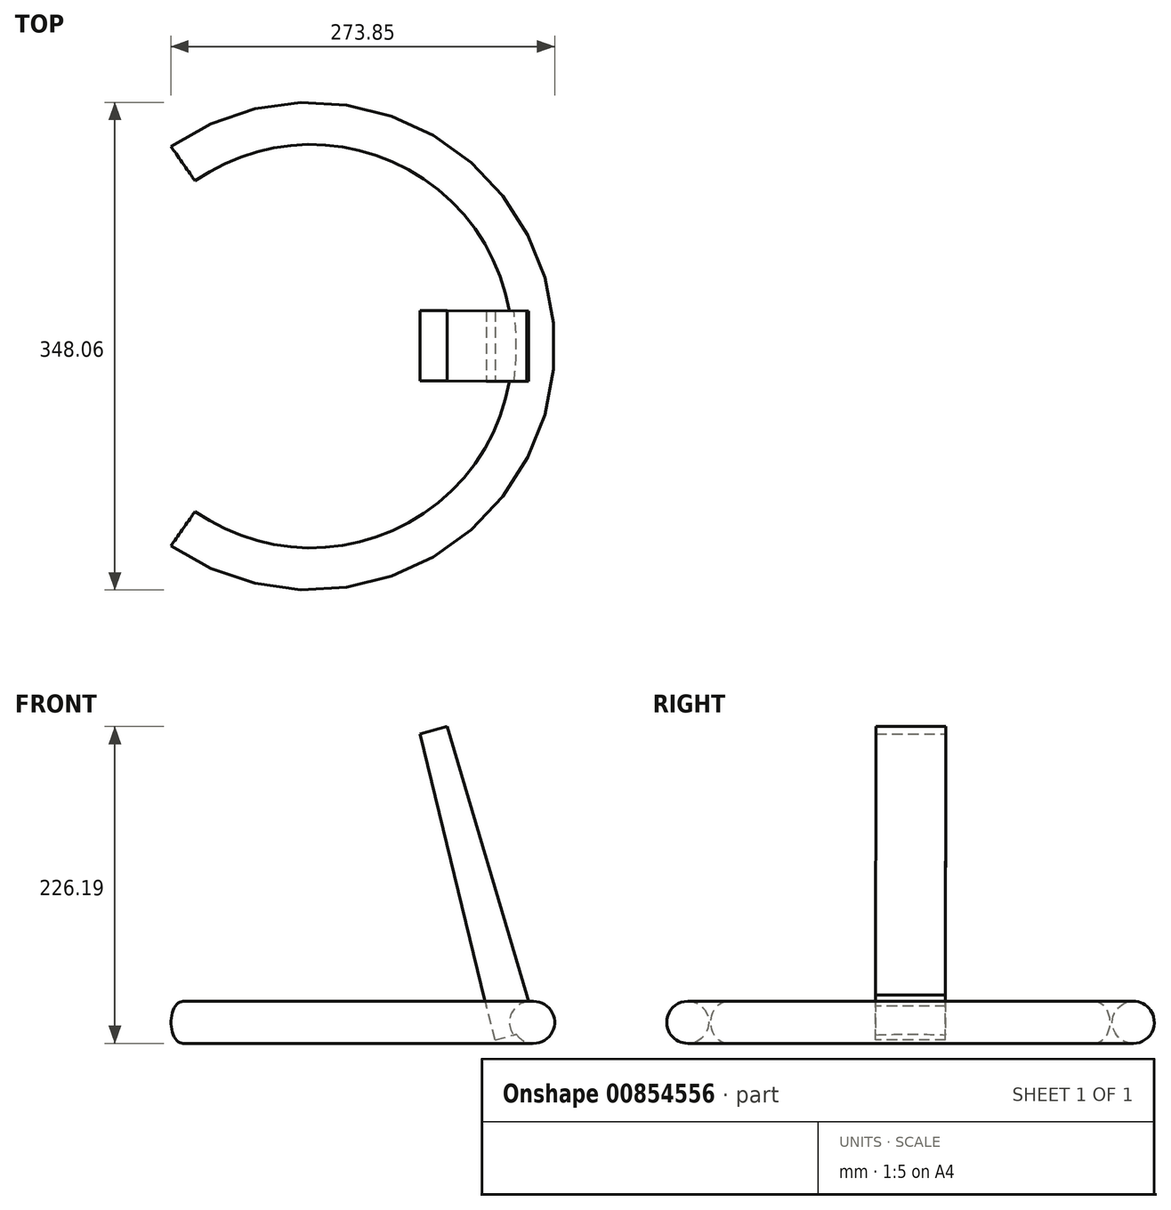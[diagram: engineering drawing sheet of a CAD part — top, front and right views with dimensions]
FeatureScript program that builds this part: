
annotation { "Feature Type Name" : "Feature", "Feature Type Description" : "" }
export const myFeature = defineFeature(function(context is Context, id is Id, definition is map)
    precondition{}
    {
        {
            var Q0;
            Q0=qCreatedBy(makeId("Front.planeOp"),FACE);
            var sketch = newSketch(context, id + "F0", { "sketchPlane" : qUnion([Q0])});
            skCircle(sketch, "E0", {"center": v(105.59, 0) * mm, "radius": 15 * mm});
            skSolve(sketch);
        }
        {
            var Q0;
            Q0=qCreatedBy(makeId("Front.planeOp"),FACE);
            var sketch = newSketch(context, id + "F1", { "sketchPlane" : qUnion([Q0])});
            skLineSegment(sketch, "E1", {"start": v(-53.44, 10.99) * mm, "end": v(-53.44, -15.19) * mm});
            skSolve(sketch);
        }
        {
            var Q0;
            Q0=qSketchRegion(id+"F0",true);
            var Q1;
            Q1=sQuery(id+"F1.wireOp",EDGE,"E1");
            revolve(context, id + "F2", {"surfaceOperationType" : NewSurfaceOperationType.NEW, "entities" : qUnion([Q0]), "axis" : qUnion([Q1]), "revolveType" : RevolveType.SYMMETRIC, "angle" : 250 * degree});
        }
        {
            var Q0;
            Q0=qCreatedBy(makeId("Top.planeOp"),FACE);
            var sketch = newSketch(context, id + "F3", { "sketchPlane" : qUnion([Q0])});
            skLineSegment(sketch, "E2.bottom", {"start": v(90, -25) * mm, "end": v(120, -25) * mm});
            skLineSegment(sketch, "E2.top", {"start": v(90, 25) * mm, "end": v(120, 25) * mm});
            skLineSegment(sketch, "E2.left", {"start": v(90, -25) * mm, "end": v(90, 25) * mm});
            skLineSegment(sketch, "E2.right", {"start": v(120, -25) * mm, "end": v(120, 25) * mm});
            skSolve(sketch);
        }
        {
            var Q0;
            Q0=qCreatedBy(makeId("Top.planeOp"),FACE);
            var sketch = newSketch(context, id + "F4", { "sketchPlane" : qUnion([Q0])});
            skLineSegment(sketch, "E3", {"start": v(28.32, 42.65) * mm, "end": v(28.32, -38.74) * mm});
            skSolve(sketch);
        }
        {
            var Q0;
            Q0=qCreatedBy(makeId("Top.planeOp"),FACE);
            var Q1;
            Q1=sQuery(id+"F4.wireOp",EDGE,"E3");
            cPlane(context, id + "F5", {"entities" : qUnion([Q0, Q1]), "cplaneType" : CPlaneType.LINE_ANGLE, "offset" : 25 * mm, "angle" : 15 * degree, "width" : 150 * mm, "height" : 150 * mm});
        }
        {
            var Q0;
            Q0=qCreatedBy(id+"F5.planeOp",FACE);
            var sketch = newSketch(context, id + "F6", { "sketchPlane" : qUnion([Q0])});
            skLineSegment(sketch, "E4.bottom", {"start": v(72.36, -25) * mm, "end": v(102.36, -25) * mm});
            skLineSegment(sketch, "E4.top", {"start": v(72.36, 25) * mm, "end": v(102.36, 25) * mm});
            skLineSegment(sketch, "E4.left", {"start": v(72.36, -25) * mm, "end": v(72.36, 25) * mm});
            skLineSegment(sketch, "E4.right", {"start": v(102.36, -25) * mm, "end": v(102.36, 25) * mm});
            skPoint(sketch, "E4.middle", {"position": v(87.36, 0) * mm});
            skSolve(sketch);
        }
        {
            var Q0;
            Q0 = qSketchRegion(id + "F6", true);
            extrude(context, id + "F7", {"entities" : qUnion([Q0]), "operationType" : NewBodyOperationType.ADD, "depth" : 25 * mm, "offsetDistance" : 25 * mm});
        }
        {
            var Q0;
            Q0=qCreatedBy(id+"F5.planeOp",FACE);
            cPlane(context, id + "F8", {"entities" : qUnion([Q0]), "cplaneType" : CPlaneType.OFFSET, "offset" : 200 * mm, "oppositeDirection" : true, "width" : 150 * mm, "height" : 150 * mm});
        }
        {
            var Q0;
            Q0=qCreatedBy(id+"F8.planeOp",FACE);
            var sketch = newSketch(context, id + "F9", { "sketchPlane" : qUnion([Q0])});
            skLineSegment(sketch, "E5.bottom", {"start": v(76.93, 24.7) * mm, "end": v(96.93, 24.7) * mm});
            skLineSegment(sketch, "E5.top", {"start": v(76.93, -25.3) * mm, "end": v(96.93, -25.3) * mm});
            skLineSegment(sketch, "E5.left", {"start": v(76.93, 24.7) * mm, "end": v(76.93, -25.3) * mm});
            skLineSegment(sketch, "E5.right", {"start": v(96.93, 24.7) * mm, "end": v(96.93, -25.3) * mm});
            skSolve(sketch);
        }
        {
            var Q1;
            Q1=makeQuery(id+"F9.imprint","IMPRINT",FACE,{"disambiguationData":[TD([[makeQuery(id+"F9.imprint","IMPRINT",EDGE,{"derivedFrom":sQuery(id+"F9.wireOp",EDGE,"E5.bottom")}),-1.0]])]});
            var Q2;
            Q2=makeQuery(id+"F7.opExtrude","CAP_FACE",FACE,{"disambiguationData":[OSD([sQuery(id+"F6.wireOp",EDGE,"E4.bottom"),sQuery(id+"F6.wireOp",EDGE,"E4.top"),sQuery(id+"F6.wireOp",EDGE,"E4.left"),sQuery(id+"F6.wireOp",EDGE,"E4.right")])],"isStart":true});
            loft(context, id + "F10", {"operationType" : NewBodyOperationType.ADD, "sheetProfilesArray" : [{ "sheetProfileEntities" : qUnion([Q1]) }, { "sheetProfileEntities" : qUnion([Q2]) }]});
        }
    });
